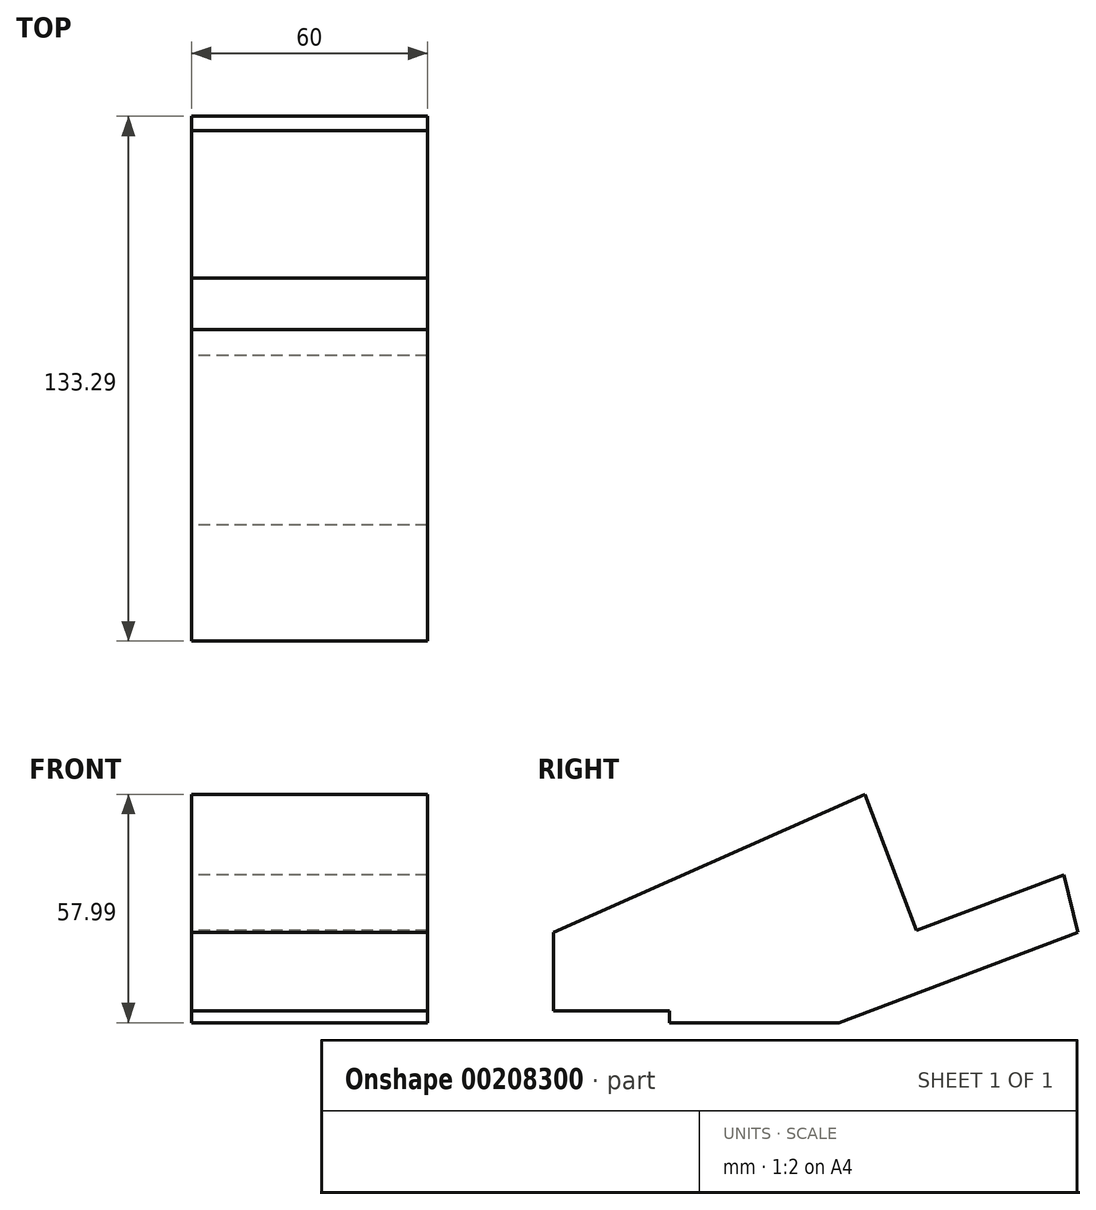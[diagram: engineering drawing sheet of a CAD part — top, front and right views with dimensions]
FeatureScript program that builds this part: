
annotation { "Feature Type Name" : "Feature", "Feature Type Description" : "" }
export const myFeature = defineFeature(function(context is Context, id is Id, definition is map)
    precondition{}
    {
        {
            var Q0;
            Q0=qCreatedBy(makeId("Right.planeOp"),FACE);
            var sketch = newSketch(context, id + "F0", { "sketchPlane" : qUnion([Q0])});
            skLineSegment(sketch, "E0", {"start": v(0, -20) * mm, "end": v(29.5, -20) * mm});
            skLineSegment(sketch, "E1", {"start": v(29.5, -20) * mm, "end": v(29.5, -23) * mm});
            skLineSegment(sketch, "E2", {"start": v(29.5, -23) * mm, "end": v(72.5, -23) * mm});
            skLineSegment(sketch, "E3", {"start": v(72.5, -23) * mm, "end": v(133.3, 0) * mm});
            skLineSegment(sketch, "E4", {"start": v(133.3, 0) * mm, "end": v(129.67, 14.55) * mm});
            skLineSegment(sketch, "E5", {"start": v(0, 0) * mm, "end": v(0, -20) * mm});
            skLineSegment(sketch, "E6", {"start": v(79.17, 35) * mm, "end": v(0, 0) * mm});
            skLineSegment(sketch, "E7", {"start": v(79.17, 35) * mm, "end": v(92.25, 0.4) * mm});
            skLineSegment(sketch, "E8", {"start": v(92.25, 0.4) * mm, "end": v(129.67, 14.55) * mm});
            skSolve(sketch);
        }
        {
            var Q0;
            Q0 = qSketchRegion(id + "F0", true);
            extrude(context, id + "F1", {"entities" : qUnion([Q0]), "depth" : 60 * mm});
        }
    });
